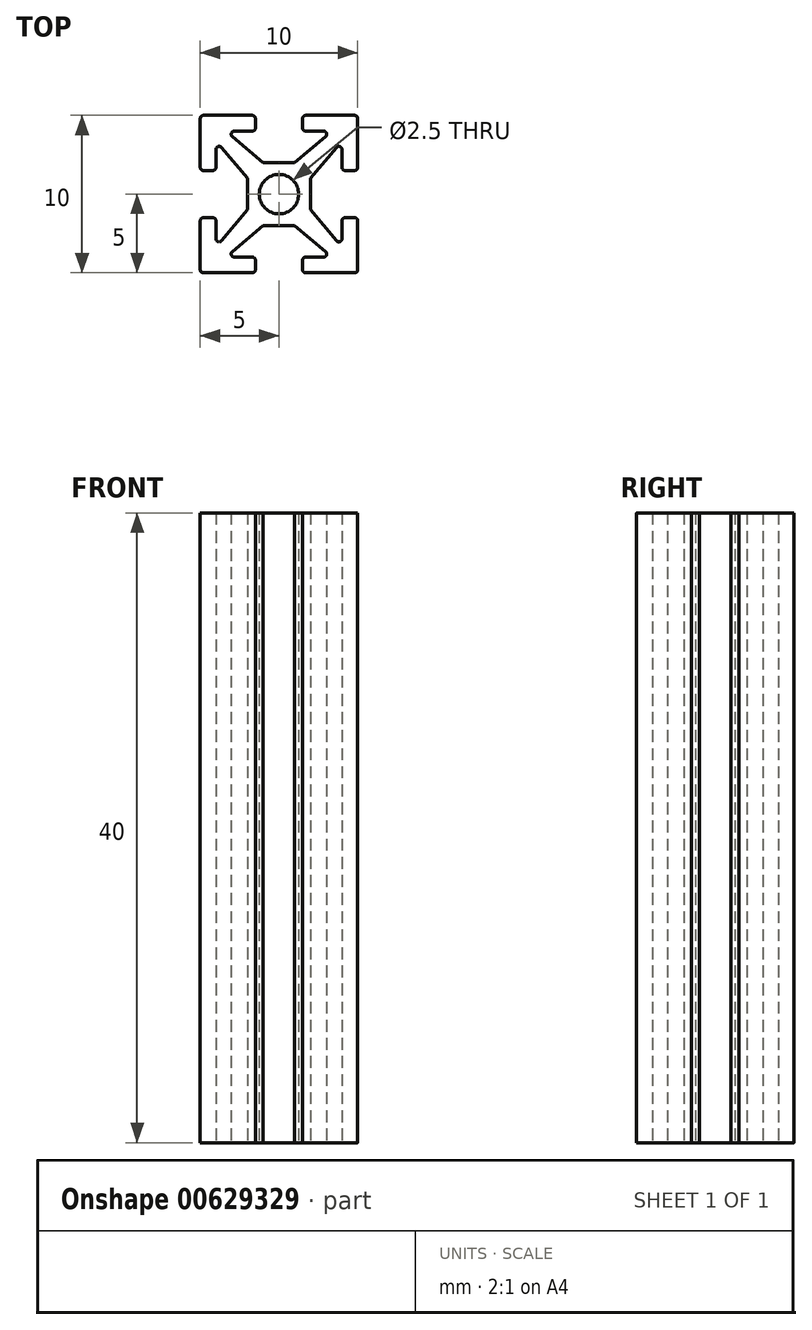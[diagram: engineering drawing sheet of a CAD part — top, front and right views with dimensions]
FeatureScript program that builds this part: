
annotation { "Feature Type Name" : "Feature", "Feature Type Description" : "" }
export const myFeature = defineFeature(function(context is Context, id is Id, definition is map)
    precondition{}
    {
        {
            var Q0;
            Q0=qCreatedBy(makeId("Top.planeOp"),FACE);
            var sketch = newSketch(context, id + "F0", { "sketchPlane" : qUnion([Q0])});
            skLineSegment(sketch, "E0", {"start": v(-2, 0) * mm, "end": v(-2, 1) * mm});
            skLineSegment(sketch, "E1", {"start": v(-2, 1) * mm, "end": v(-3.65, 2.96) * mm});
            skLineSegment(sketch, "E2", {"start": v(-4, 2.83) * mm, "end": v(-4, 1.7) * mm});
            skLineSegment(sketch, "E3", {"start": v(-4.2, 1.5) * mm, "end": v(-4.8, 1.5) * mm});
            skLineSegment(sketch, "E4", {"start": v(-5, 1.7) * mm, "end": v(-5, 4.8) * mm});
            skLineSegment(sketch, "E5", {"start": v(0, 0) * mm, "end": v(-5, 5) * mm, "construction": true});
            skArc(sketch, "E6.filletArc", {"start": v(-5, 1.7) * mm, "mid": v(-4.94, 1.56) * mm, "end": v(-4.8, 1.5) * mm});
            skPoint(sketch, "E7.visualSharp", {"position": v(-4, 1.5) * mm});
            skArc(sketch, "E7.filletArc", {"start": v(-4.2, 1.5) * mm, "mid": v(-4.06, 1.56) * mm, "end": v(-4, 1.7) * mm});
            skPoint(sketch, "E8.visualSharp", {"position": v(-4, 3.38) * mm});
            skArc(sketch, "E8.filletArc", {"start": v(-3.65, 2.96) * mm, "mid": v(-3.87, 3.02) * mm, "end": v(-4, 2.83) * mm});
            skArc(sketch, "E9", {"start": v(-5, 4.8) * mm, "mid": v(-4.98, 4.88) * mm, "end": v(-4.94, 4.94) * mm});
            skArc(sketch, "E10.MirrorCS", {"start": v(-4.8, 5) * mm, "mid": v(-4.88, 4.98) * mm, "end": v(-4.94, 4.94) * mm});
            skLineSegment(sketch, "E11.MirrorCS", {"start": v(-1.7, 5) * mm, "end": v(-4.8, 5) * mm});
            skArc(sketch, "E12.MirrorCS", {"start": v(-1.7, 5) * mm, "mid": v(-1.56, 4.94) * mm, "end": v(-1.5, 4.8) * mm});
            skLineSegment(sketch, "E13.MirrorCS", {"start": v(-1.5, 4.2) * mm, "end": v(-1.5, 4.8) * mm});
            skArc(sketch, "E14.MirrorCS", {"start": v(-1.5, 4.2) * mm, "mid": v(-1.56, 4.06) * mm, "end": v(-1.7, 4) * mm});
            skLineSegment(sketch, "E15.MirrorCS", {"start": v(-2.83, 4) * mm, "end": v(-1.7, 4) * mm});
            skArc(sketch, "E16.MirrorCS", {"start": v(-2.96, 3.65) * mm, "mid": v(-3.02, 3.87) * mm, "end": v(-2.83, 4) * mm});
            skLineSegment(sketch, "E17.MirrorCS", {"start": v(-1, 2) * mm, "end": v(-2.96, 3.65) * mm});
            skLineSegment(sketch, "E18.MirrorCS", {"start": v(0, 2) * mm, "end": v(-1, 2) * mm});
            skLineSegment(sketch, "E19.MirrorCS", {"start": v(0, 2) * mm, "end": v(1, 2) * mm});
            skLineSegment(sketch, "E20.MirrorCS", {"start": v(1, 2) * mm, "end": v(2.96, 3.65) * mm});
            skArc(sketch, "E21.MirrorCS", {"start": v(2.96, 3.65) * mm, "mid": v(3.02, 3.87) * mm, "end": v(2.83, 4) * mm});
            skLineSegment(sketch, "E22.MirrorCS", {"start": v(2.83, 4) * mm, "end": v(1.7, 4) * mm});
            skArc(sketch, "E23.MirrorCS", {"start": v(1.5, 4.2) * mm, "mid": v(1.56, 4.06) * mm, "end": v(1.7, 4) * mm});
            skLineSegment(sketch, "E24.MirrorCS", {"start": v(1.5, 4.2) * mm, "end": v(1.5, 4.8) * mm});
            skArc(sketch, "E25.MirrorCS", {"start": v(1.7, 5) * mm, "mid": v(1.56, 4.94) * mm, "end": v(1.5, 4.8) * mm});
            skLineSegment(sketch, "E26.MirrorCS", {"start": v(1.7, 5) * mm, "end": v(4.8, 5) * mm});
            skArc(sketch, "E27.MirrorCS", {"start": v(4.8, 5) * mm, "mid": v(4.88, 4.98) * mm, "end": v(4.94, 4.94) * mm});
            skArc(sketch, "E28.MirrorCS", {"start": v(5, 4.8) * mm, "mid": v(4.98, 4.88) * mm, "end": v(4.94, 4.94) * mm});
            skLineSegment(sketch, "E29.MirrorCS", {"start": v(5, 1.7) * mm, "end": v(5, 4.8) * mm});
            skArc(sketch, "E30.MirrorCS", {"start": v(5, 1.7) * mm, "mid": v(4.94, 1.56) * mm, "end": v(4.8, 1.5) * mm});
            skLineSegment(sketch, "E31.MirrorCS", {"start": v(4.2, 1.5) * mm, "end": v(4.8, 1.5) * mm});
            skArc(sketch, "E32.MirrorCS", {"start": v(4.2, 1.5) * mm, "mid": v(4.06, 1.56) * mm, "end": v(4, 1.7) * mm});
            skLineSegment(sketch, "E33.MirrorCS", {"start": v(4, 2.83) * mm, "end": v(4, 1.7) * mm});
            skArc(sketch, "E34.MirrorCS", {"start": v(3.65, 2.96) * mm, "mid": v(3.87, 3.02) * mm, "end": v(4, 2.83) * mm});
            skLineSegment(sketch, "E35.MirrorCS", {"start": v(2, 1) * mm, "end": v(3.65, 2.96) * mm});
            skLineSegment(sketch, "E36.MirrorCS", {"start": v(2, 0) * mm, "end": v(2, 1) * mm});
            skLineSegment(sketch, "E37.MirrorCS", {"start": v(-2, 0) * mm, "end": v(-2, -1) * mm});
            skLineSegment(sketch, "E38.MirrorCS", {"start": v(-2, -1) * mm, "end": v(-3.65, -2.96) * mm});
            skArc(sketch, "E39.MirrorCS", {"start": v(-3.65, -2.96) * mm, "mid": v(-3.87, -3.02) * mm, "end": v(-4, -2.83) * mm});
            skLineSegment(sketch, "E40.MirrorCS", {"start": v(-4, -2.83) * mm, "end": v(-4, -1.7) * mm});
            skArc(sketch, "E41.MirrorCS", {"start": v(-4.2, -1.5) * mm, "mid": v(-4.06, -1.56) * mm, "end": v(-4, -1.7) * mm});
            skLineSegment(sketch, "E42.MirrorCS", {"start": v(-4.2, -1.5) * mm, "end": v(-4.8, -1.5) * mm});
            skArc(sketch, "E43.MirrorCS", {"start": v(-5, -1.7) * mm, "mid": v(-4.94, -1.56) * mm, "end": v(-4.8, -1.5) * mm});
            skLineSegment(sketch, "E44.MirrorCS", {"start": v(-5, -1.7) * mm, "end": v(-5, -4.8) * mm});
            skArc(sketch, "E45.MirrorCS", {"start": v(-5, -4.8) * mm, "mid": v(-4.98, -4.88) * mm, "end": v(-4.94, -4.94) * mm});
            skArc(sketch, "E46.MirrorCS", {"start": v(-4.8, -5) * mm, "mid": v(-4.88, -4.98) * mm, "end": v(-4.94, -4.94) * mm});
            skLineSegment(sketch, "E47.MirrorCS", {"start": v(-1.7, -5) * mm, "end": v(-4.8, -5) * mm});
            skArc(sketch, "E48.MirrorCS", {"start": v(-1.7, -5) * mm, "mid": v(-1.56, -4.94) * mm, "end": v(-1.5, -4.8) * mm});
            skLineSegment(sketch, "E49.MirrorCS", {"start": v(-1.5, -4.2) * mm, "end": v(-1.5, -4.8) * mm});
            skArc(sketch, "E50.MirrorCS", {"start": v(-1.5, -4.2) * mm, "mid": v(-1.56, -4.06) * mm, "end": v(-1.7, -4) * mm});
            skLineSegment(sketch, "E51.MirrorCS", {"start": v(-2.83, -4) * mm, "end": v(-1.7, -4) * mm});
            skArc(sketch, "E52.MirrorCS", {"start": v(-2.96, -3.65) * mm, "mid": v(-3.02, -3.87) * mm, "end": v(-2.83, -4) * mm});
            skLineSegment(sketch, "E53.MirrorCS", {"start": v(-1, -2) * mm, "end": v(-2.96, -3.65) * mm});
            skLineSegment(sketch, "E54.MirrorCS", {"start": v(0, -2) * mm, "end": v(-1, -2) * mm});
            skLineSegment(sketch, "E55.MirrorCS", {"start": v(0, -2) * mm, "end": v(1, -2) * mm});
            skLineSegment(sketch, "E56.MirrorCS", {"start": v(1, -2) * mm, "end": v(2.96, -3.65) * mm});
            skArc(sketch, "E57.MirrorCS", {"start": v(2.96, -3.65) * mm, "mid": v(3.02, -3.87) * mm, "end": v(2.83, -4) * mm});
            skLineSegment(sketch, "E58.MirrorCS", {"start": v(2.83, -4) * mm, "end": v(1.7, -4) * mm});
            skArc(sketch, "E59.MirrorCS", {"start": v(1.5, -4.2) * mm, "mid": v(1.56, -4.06) * mm, "end": v(1.7, -4) * mm});
            skLineSegment(sketch, "E60.MirrorCS", {"start": v(1.5, -4.2) * mm, "end": v(1.5, -4.8) * mm});
            skArc(sketch, "E61.MirrorCS", {"start": v(1.7, -5) * mm, "mid": v(1.56, -4.94) * mm, "end": v(1.5, -4.8) * mm});
            skLineSegment(sketch, "E62.MirrorCS", {"start": v(1.7, -5) * mm, "end": v(4.8, -5) * mm});
            skArc(sketch, "E63.MirrorCS", {"start": v(4.8, -5) * mm, "mid": v(4.88, -4.98) * mm, "end": v(4.94, -4.94) * mm});
            skArc(sketch, "E64.MirrorCS", {"start": v(5, -4.8) * mm, "mid": v(4.98, -4.88) * mm, "end": v(4.94, -4.94) * mm});
            skLineSegment(sketch, "E65.MirrorCS", {"start": v(5, -1.7) * mm, "end": v(5, -4.8) * mm});
            skArc(sketch, "E66.MirrorCS", {"start": v(5, -1.7) * mm, "mid": v(4.94, -1.56) * mm, "end": v(4.8, -1.5) * mm});
            skLineSegment(sketch, "E67.MirrorCS", {"start": v(4.2, -1.5) * mm, "end": v(4.8, -1.5) * mm});
            skArc(sketch, "E68.MirrorCS", {"start": v(4.2, -1.5) * mm, "mid": v(4.06, -1.56) * mm, "end": v(4, -1.7) * mm});
            skLineSegment(sketch, "E69.MirrorCS", {"start": v(4, -2.83) * mm, "end": v(4, -1.7) * mm});
            skArc(sketch, "E70.MirrorCS", {"start": v(3.65, -2.96) * mm, "mid": v(3.87, -3.02) * mm, "end": v(4, -2.83) * mm});
            skLineSegment(sketch, "E71.MirrorCS", {"start": v(2, -1) * mm, "end": v(3.65, -2.96) * mm});
            skLineSegment(sketch, "E72.MirrorCS", {"start": v(2, 0) * mm, "end": v(2, -1) * mm});
            skCircle(sketch, "E73", {"center": v(0, 0) * mm, "radius": 1.25 * mm});
            skSolve(sketch);
        }
        {
            var Q0;
            Q0=makeQuery(id+"F0.imprint","IMPRINT",FACE,{"disambiguationData":[TD([[makeQuery(id+"F0.imprint","IMPRINT",EDGE,{"derivedFrom":sQuery(id+"F0.wireOp",EDGE,"E0")}),-1.0]])]});
            extrude(context, id + "F1", {"entities" : qUnion([Q0]), "endBound" : BoundingType.SYMMETRIC, "depth" : 40 * mm, "offsetDistance" : 25 * mm});
        }
    });
